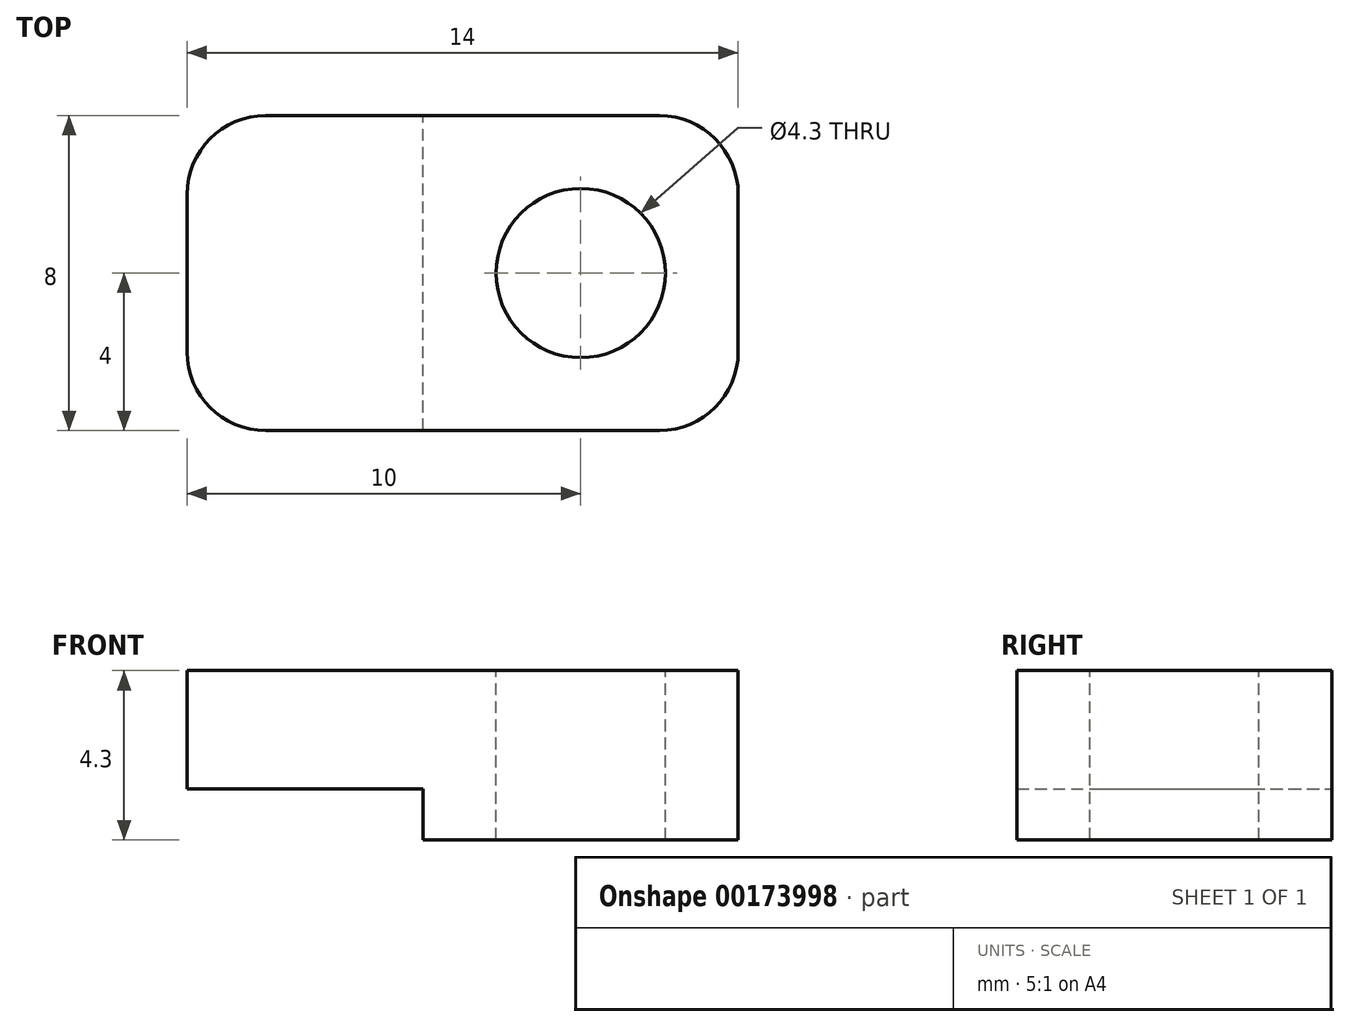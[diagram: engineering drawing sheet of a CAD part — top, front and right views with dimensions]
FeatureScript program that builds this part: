
annotation { "Feature Type Name" : "Feature", "Feature Type Description" : "" }
export const myFeature = defineFeature(function(context is Context, id is Id, definition is map)
    precondition{}
    {
        {
            assignVariable(context, id + "F0", {"name" : "filletMinor", "anyValue" : 2});
        }
        {
            var Q0;
            Q0=qCreatedBy(makeId("Front.planeOp"),FACE);
            var sketch = newSketch(context, id + "F1", { "sketchPlane" : qUnion([Q0])});
            skLineSegment(sketch, "E0", {"start": v(6, -4.3) * mm, "end": v(6, -3) * mm});
            skLineSegment(sketch, "E1", {"start": v(6, -3) * mm, "end": v(0, -3) * mm});
            skLineSegment(sketch, "E2", {"start": v(0, -3) * mm, "end": v(0, 0) * mm});
            skLineSegment(sketch, "E3", {"start": v(0, 0) * mm, "end": v(14, 0) * mm});
            skLineSegment(sketch, "E4", {"start": v(14, 0) * mm, "end": v(14, -4.3) * mm});
            skLineSegment(sketch, "E5", {"start": v(14, -4.3) * mm, "end": v(6, -4.3) * mm});
            skSolve(sketch);
        }
        {
            var Q0;
            Q0 = qSketchRegion(id + "F1", true);
            extrude(context, id + "F2", {"entities" : qUnion([Q0]), "depth" : 8 * mm});
        }
        {
            var Q0;
            Q0=makeQuery(id+"F2.opExtrude","SWEPT_FACE",FACE,{"disambiguationData":[OSD([sQuery(id+"F1.wireOp",EDGE,"E3")])]});
            var sketch = newSketch(context, id + "F3", { "sketchPlane" : qUnion([Q0])});
            skCircle(sketch, "E6", {"center": v(10, -4) * mm, "radius": 2.15 * mm});
            skPoint(sketch, "E6.centerSnap0", {"position": v(14, -4) * mm});
            skLineSegment(sketch, "E7.0", {"start": v(6, -8) * mm, "end": v(6, 0) * mm, "construction": true});
            skLineSegment(sketch, "E8", {"start": v(6, -8) * mm, "end": v(14, -8) * mm, "construction": true});
            skPoint(sketch, "E9", {"position": v(10, -8) * mm});
            skSolve(sketch);
        }
        {
            var Q0;
            Q0 = qSketchRegion(id + "F3", true);
            extrude(context, id + "F4", {"entities" : qUnion([Q0]), "operationType" : NewBodyOperationType.REMOVE, "endBound" : BoundingType.UP_TO_NEXT, "oppositeDirection" : true, "depth" : 25 * mm});
        }
        {
            var Q0;
            Q0=makeQuery(id+"F2.opExtrude","CAP_EDGE",EDGE,{"disambiguationData":[OSD([sQuery(id+"F1.wireOp",EDGE,"E4")])],"isStart":false});
            var Q1;
            Q1=makeQuery(id+"F2.opExtrude","CAP_EDGE",EDGE,{"disambiguationData":[OSD([sQuery(id+"F1.wireOp",EDGE,"E4")])],"isStart":true});
            var Q2;
            Q2=makeQuery(id+"F2.opExtrude","CAP_EDGE",EDGE,{"disambiguationData":[OSD([sQuery(id+"F1.wireOp",EDGE,"E2")])],"isStart":false});
            var Q3;
            Q3=makeQuery(id+"F2.opExtrude","CAP_EDGE",EDGE,{"disambiguationData":[OSD([sQuery(id+"F1.wireOp",EDGE,"E2")])],"isStart":true});
            var Q4;
            Q4=makeQuery(id+"F2.opExtrude","CAP_EDGE",EDGE,{"disambiguationData":[OSD([sQuery(id+"F1.wireOp",EDGE,"lUWiY6BN-h0J2-r0Aj-D8QP-xYxvZGp5HKe7")])],"isStart":false});
            var Q5;
            Q5=makeQuery(id+"F2.opExtrude","CAP_EDGE",EDGE,{"disambiguationData":[OSD([sQuery(id+"F1.wireOp",EDGE,"lUWiY6BN-h0J2-r0Aj-D8QP-xYxvZGp5HKe7")])],"isStart":true});
            fillet(context, id + "F5", {"entities" : qUnion([Q0, Q1, Q2, Q3, Q4, Q5]), "radius" : (getVariable(context, 'filletMinor')) * mm, "tangentPropagation" : true, "allowEdgeOverflow" : false});
        }
    });
